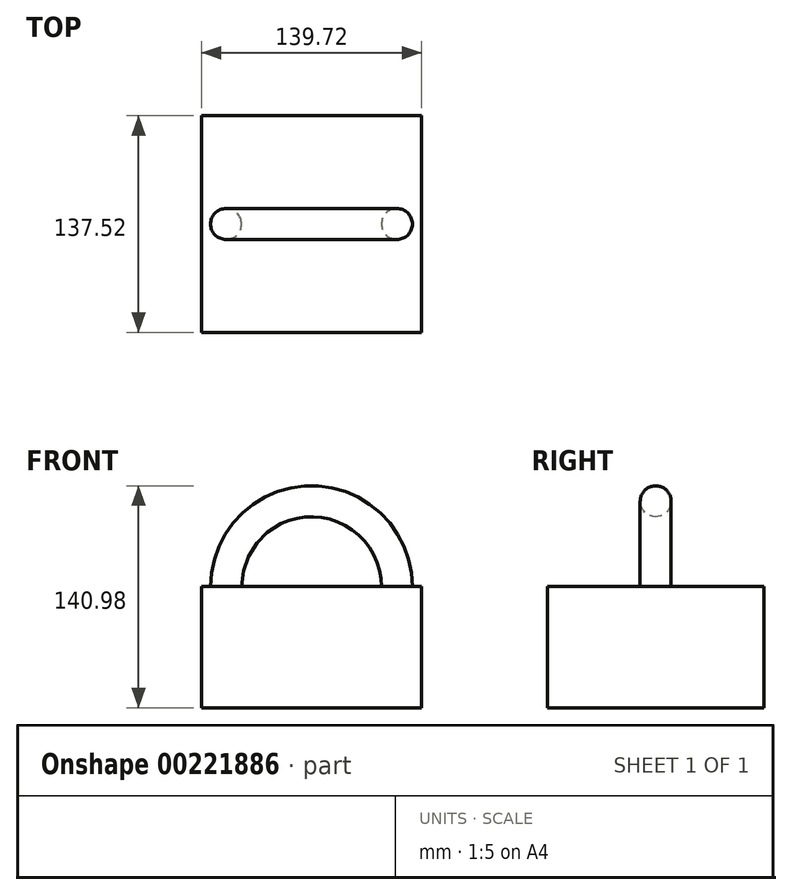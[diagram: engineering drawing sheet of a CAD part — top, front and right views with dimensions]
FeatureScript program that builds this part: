
annotation { "Feature Type Name" : "Feature", "Feature Type Description" : "" }
export const myFeature = defineFeature(function(context is Context, id is Id, definition is map)
    precondition{}
    {
        {
            var Q0;
            Q0=qCreatedBy(makeId("Top.planeOp"),FACE);
            var sketch = newSketch(context, id + "F0", { "sketchPlane" : qUnion([Q0])});
            skLineSegment(sketch, "E0.bottom", {"start": v(69.86, -68.76) * mm, "end": v(-69.86, -68.76) * mm});
            skLineSegment(sketch, "E0.top", {"start": v(69.86, 68.76) * mm, "end": v(-69.86, 68.76) * mm});
            skLineSegment(sketch, "E0.left", {"start": v(69.86, -68.76) * mm, "end": v(69.86, 68.76) * mm});
            skLineSegment(sketch, "E0.right", {"start": v(-69.86, -68.76) * mm, "end": v(-69.86, 68.76) * mm});
            skPoint(sketch, "E0.middle", {"position": v(0, 0) * mm});
            skLineSegment(sketch, "E1", {"start": v(0, 68.76) * mm, "end": v(0, -68.76) * mm});
            skSolve(sketch);
        }
        {
            var Q0;
            Q0=qCreatedBy(makeId("Top.planeOp"),FACE);
            var sketch = newSketch(context, id + "F1", { "sketchPlane" : qUnion([Q0])});
            skCircle(sketch, "E2", {"center": v(54.26, 0) * mm, "radius": 9.82 * mm});
            skSolve(sketch);
        }
        {
            var Q0;
            Q0 = qSketchRegion(id + "F0", true);
            extrude(context, id + "F2", {"entities" : qUnion([Q0]), "oppositeDirection" : true, "depth" : 76.89 * mm});
        }
        {
            var Q0;
            Q0 = qSketchRegion(id + "F1", true);
            var Q1;
            Q1=sQuery(id+"F0.wireOp",EDGE,"E1");
            revolve(context, id + "F3", {"operationType" : NewBodyOperationType.ADD, "entities" : qUnion([Q0]), "axis" : qUnion([Q1]), "revolveType" : RevolveType.FULL});
        }
    });
